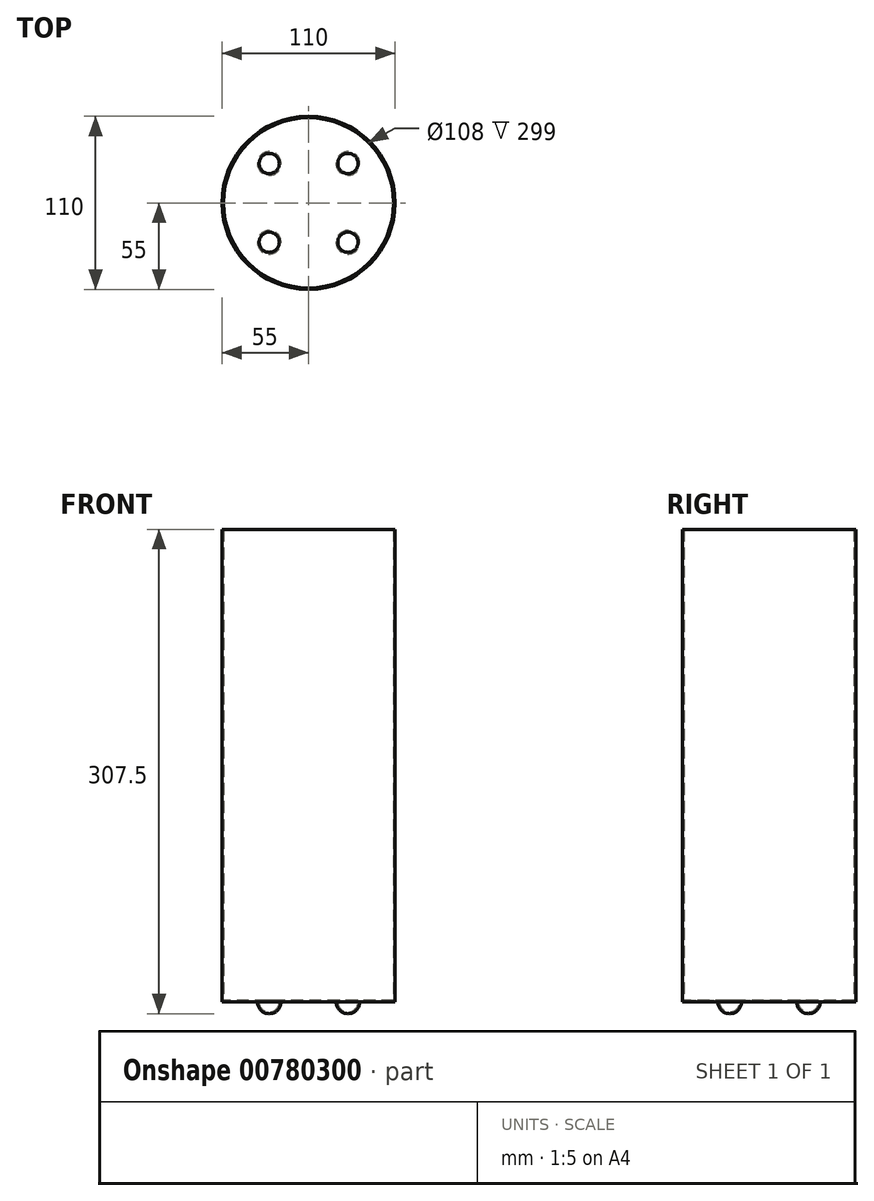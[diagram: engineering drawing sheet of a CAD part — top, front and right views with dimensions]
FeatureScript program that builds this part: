
annotation { "Feature Type Name" : "Feature", "Feature Type Description" : "" }
export const myFeature = defineFeature(function(context is Context, id is Id, definition is map)
    precondition{}
    {
        {
            var Q0;
            Q0=qCreatedBy(makeId("Top.planeOp"),FACE);
            var sketch = newSketch(context, id + "F0", { "sketchPlane" : qUnion([Q0])});
            skCircle(sketch, "E0", {"center": v(0, 0) * mm, "radius": 55 * mm});
            skSolve(sketch);
        }
        {
            var Q0;
            Q0=makeQuery(id+"F0.imprint","IMPRINT",FACE,{"disambiguationData":[TD([[makeQuery(id+"F0.imprint","IMPRINT",EDGE,{"derivedFrom":sQuery(id+"F0.wireOp",EDGE,"E0")}),1.0]])]});
            extrude(context, id + "F1", {"entities" : qUnion([Q0]), "depth" : 300 * mm, "offsetDistance" : 25 * mm});
        }
        {
            var Q0;
            Q0=makeQuery(id+"F1.opExtrude","CAP_FACE",FACE,{"disambiguationData":[OSD([sQuery(id+"F0.wireOp",EDGE,"E0")])],"isStart":true});
            var sketch = newSketch(context, id + "F2", { "sketchPlane" : qUnion([Q0])});
            skPoint(sketch, "E1.middle", {"position": v(0, 0) * mm});
            skArc(sketch, "E2", {"start": v(32.5, 25) * mm, "mid": v(25, 32.5) * mm, "end": v(17.5, 25) * mm});
            skArc(sketch, "E3", {"start": v(-17.5, 25) * mm, "mid": v(-25, 32.5) * mm, "end": v(-32.5, 25) * mm});
            skArc(sketch, "E4", {"start": v(-17.5, -25) * mm, "mid": v(-25, -17.5) * mm, "end": v(-32.5, -25) * mm});
            skArc(sketch, "E5", {"start": v(32.5, -25) * mm, "mid": v(25, -17.5) * mm, "end": v(17.5, -25) * mm});
            skLineSegment(sketch, "E6", {"start": v(-32.5, -25) * mm, "end": v(-17.5, -25) * mm});
            skLineSegment(sketch, "E7", {"start": v(-32.5, 25) * mm, "end": v(-17.5, 25) * mm});
            skLineSegment(sketch, "E8", {"start": v(25, -25) * mm, "end": v(17.5, -25) * mm});
            skLineSegment(sketch, "E9", {"start": v(17.5, -25) * mm, "end": v(32.5, -25) * mm});
            skLineSegment(sketch, "E10", {"start": v(17.5, 25) * mm, "end": v(32.5, 25) * mm});
            skSolve(sketch);
        }
        {
            var Q0;
            Q0=makeQuery(id+"F2.imprint","IMPRINT",FACE,{"disambiguationData":[TD([[makeQuery(id+"F2.imprint","IMPRINT",EDGE,{"derivedFrom":sQuery(id+"F2.wireOp",EDGE,"E4")}),1.0]])]});
            var Q1;
            Q1=sQuery(id+"F2.wireOp",EDGE,"E6");
            revolve(context, id + "F3", {"operationType" : NewBodyOperationType.ADD, "surfaceOperationType" : NewSurfaceOperationType.NEW, "entities" : qUnion([Q0]), "axis" : qUnion([Q1]), "revolveType" : RevolveType.FULL});
        }
        {
            var Q0;
            Q0=makeQuery(id+"F2.imprint","IMPRINT",FACE,{"disambiguationData":[TD([[makeQuery(id+"F2.imprint","IMPRINT",EDGE,{"derivedFrom":sQuery(id+"F2.wireOp",EDGE,"E3")}),1.0]])]});
            var Q1;
            Q1=sQuery(id+"F2.wireOp",EDGE,"E7");
            revolve(context, id + "F4", {"operationType" : NewBodyOperationType.ADD, "surfaceOperationType" : NewSurfaceOperationType.NEW, "entities" : qUnion([Q0]), "axis" : qUnion([Q1]), "revolveType" : RevolveType.FULL});
        }
        {
            var Q0;
            {var subQ0=sQuery(id+"F2.wireOp",EDGE,"E5");Q0=makeQuery(id+"F2.imprint","IMPRINT",FACE,{"disambiguationData":[TD([[makeQuery(id+"F2.imprint","IMPRINT",EDGE,{"derivedFrom":subQ0}),1.0]])]});}
            var Q1;
            Q1=sQuery(id+"F2.wireOp",EDGE,"E9");
            revolve(context, id + "F5", {"operationType" : NewBodyOperationType.ADD, "surfaceOperationType" : NewSurfaceOperationType.NEW, "entities" : qUnion([Q0]), "axis" : qUnion([Q1]), "revolveType" : RevolveType.FULL});
        }
        {
            var Q0;
            Q0=makeQuery(id+"F2.imprint","IMPRINT",FACE,{"disambiguationData":[TD([[makeQuery(id+"F2.imprint","IMPRINT",EDGE,{"derivedFrom":sQuery(id+"F2.wireOp",EDGE,"E2")}),1.0]])]});
            var Q1;
            Q1=sQuery(id+"F2.wireOp",EDGE,"E10");
            revolve(context, id + "F6", {"operationType" : NewBodyOperationType.ADD, "surfaceOperationType" : NewSurfaceOperationType.NEW, "entities" : qUnion([Q0]), "axis" : qUnion([Q1]), "revolveType" : RevolveType.FULL});
        }
        {
            var Q0;
            Q0=makeQuery(id+"F1.opExtrude","CAP_FACE",FACE,{"disambiguationData":[OSD([sQuery(id+"F0.wireOp",EDGE,"E0")])],"isStart":false});
            shell(context, id + "F7", {"entities" : qUnion([Q0]), "thickness" : 1 * mm});
        }
    });
